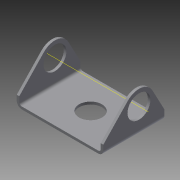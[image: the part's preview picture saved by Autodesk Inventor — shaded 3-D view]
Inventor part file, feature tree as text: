
AUTODESK INVENTOR PART (.ipt)
format: ipt  version: 2013 (Build 170138000, 138)  size: 197,120 bytes
history: native  units: in
note: dims shown in document units (in); Inventor stores cm internally (conversion verified against a paired STEP export)
features: other x8, sheet_metal_op x7, sketch x5
ambient origin geometry x8: Origin, YZ Plane, XZ Plane, XY Plane, X Axis, Y Axis, Z Axis, Center Point
bodies: Solid1 (feature_tree)
feature tree (20):
  sheet_metal_op  "Face1"
  sheet_metal_op  "Flange1"
  sheet_metal_op  "Flange2"
  other  "Work Axis1"
  sketch  "Sketch1"  dims[d0=4.0in]
  other  "Plate1"
  sketch  "Sketch2"  dims[d2=3.0in]
  other  "Plate2"
  sheet_metal_op  "Bend1"
  sheet_metal_op  "Corner1"
  sketch  "Sketch3"  dims[d3=0.125in]
  other  "Plate3"
  sheet_metal_op  "Bend2"
  sheet_metal_op  "Corner2"
  sketch  "Sketch4"  dims[d4=0.125in]
  sketch  "Sketch6"  dims[d5=0.0625in d6=0.25in d7=0.125in d8=2.0in d9=90.0deg d10=0.125in d11=0.5in d12=0.125in d13=0.125in d14=0.125in d15=0.0625in d16=0.25in d17=0.125in d18=2.0in d19=90.0deg d20=0.125in d21=0.5in d22=0.125in d23=0.125in d24=1.125in d25=0.75in d26=200.0in d27=0.0in d28=0.25in d29=0.25in d30=20.0in d31=0.0in d32=1.125in d33=0.125in d34=0.0in d35=1.5in d36=1.875in]
  other  "Cut1"
  other  "Cut2"
  other  "Cut3"
  other  "Definition1"
